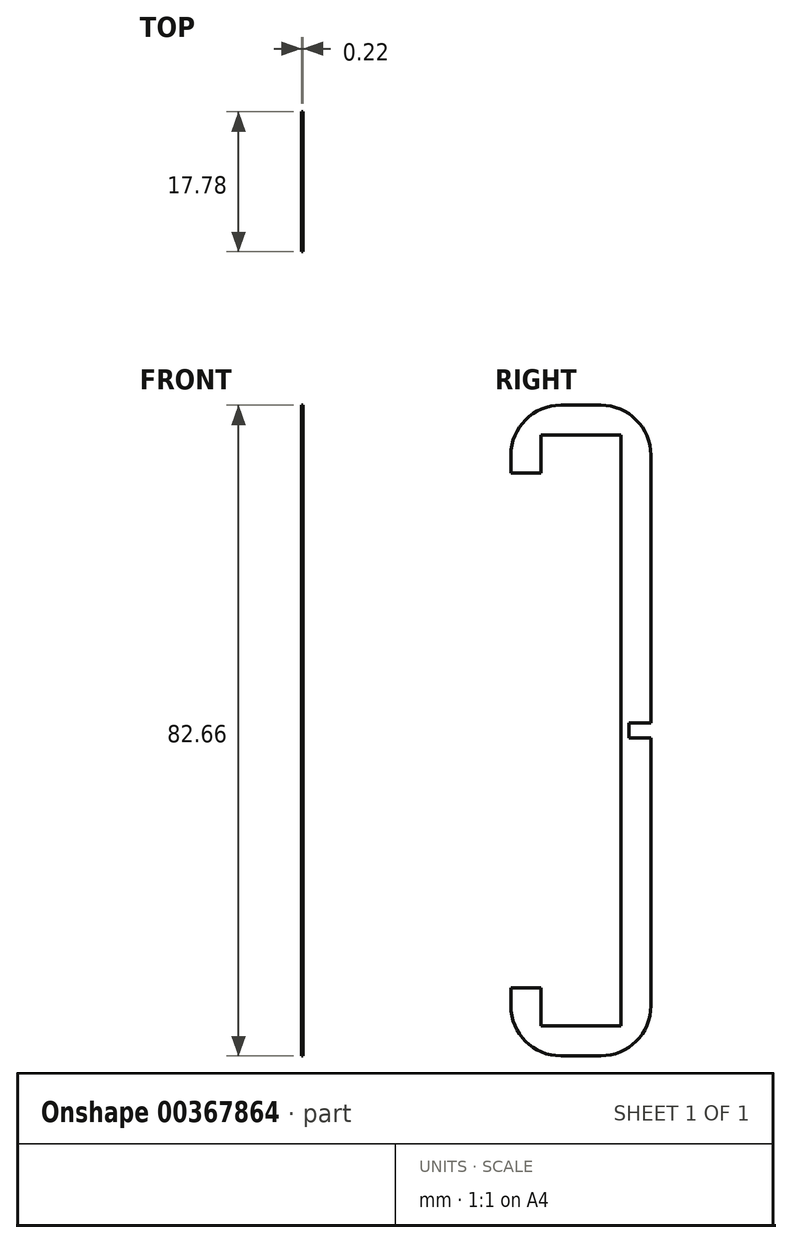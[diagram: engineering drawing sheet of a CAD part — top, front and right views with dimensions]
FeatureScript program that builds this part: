
annotation { "Feature Type Name" : "Feature", "Feature Type Description" : "" }
export const myFeature = defineFeature(function(context is Context, id is Id, definition is map)
    precondition{}
    {
        {
            var Q0;
            Q0=qCreatedBy(makeId("Right.planeOp"),FACE);
            var sketch = newSketch(context, id + "F0", { "sketchPlane" : qUnion([Q0])});
            skLineSegment(sketch, "E0", {"start": v(-8, 0) * mm, "end": v(-8, 37.52) * mm});
            skLineSegment(sketch, "E1", {"start": v(-8, 37.52) * mm, "end": v(-18.17, 37.52) * mm});
            skLineSegment(sketch, "E2", {"start": v(-18.17, 37.52) * mm, "end": v(-18.17, 32.7) * mm});
            skLineSegment(sketch, "E3", {"start": v(-18.17, 32.7) * mm, "end": v(-21.98, 32.7) * mm});
            skLineSegment(sketch, "E4", {"start": v(-21.98, 32.7) * mm, "end": v(-21.98, 34.98) * mm});
            skLineSegment(sketch, "E5", {"start": v(-15.63, 41.33) * mm, "end": v(-10.55, 41.33) * mm});
            skLineSegment(sketch, "E6", {"start": v(-4.2, 34.98) * mm, "end": v(-4.2, 0) * mm});
            skPoint(sketch, "E7.visualSharp", {"position": v(-21.98, 41.33) * mm});
            skArc(sketch, "E7.filletArc", {"start": v(-15.63, 41.33) * mm, "mid": v(-20.12, 39.47) * mm, "end": v(-21.98, 34.98) * mm});
            skPoint(sketch, "E8.visualSharp", {"position": v(-4.2, 41.33) * mm});
            skArc(sketch, "E8.filletArc", {"start": v(-4.2, 34.98) * mm, "mid": v(-6.06, 39.47) * mm, "end": v(-10.55, 41.33) * mm});
            skLineSegment(sketch, "E9.MirrorCS", {"start": v(-18.17, -37.52) * mm, "end": v(-18.17, -32.7) * mm});
            skLineSegment(sketch, "E10.MirrorCS", {"start": v(-21.98, -32.7) * mm, "end": v(-21.98, -34.98) * mm});
            skLineSegment(sketch, "E11.MirrorCS", {"start": v(-8, -37.52) * mm, "end": v(-18.17, -37.52) * mm});
            skPoint(sketch, "E12.MirrorP", {"position": v(-4.2, -41.33) * mm});
            skArc(sketch, "E13.MirrorCS", {"start": v(-15.63, -41.33) * mm, "mid": v(-20.12, -39.47) * mm, "end": v(-21.98, -34.98) * mm});
            skLineSegment(sketch, "E14.MirrorCS", {"start": v(-18.17, -32.7) * mm, "end": v(-21.98, -32.7) * mm});
            skArc(sketch, "E15.MirrorCS", {"start": v(-4.2, -34.98) * mm, "mid": v(-6.06, -39.47) * mm, "end": v(-10.55, -41.33) * mm});
            skPoint(sketch, "E16.MirrorP", {"position": v(-21.98, -41.33) * mm});
            skLineSegment(sketch, "E17.MirrorCS", {"start": v(-15.63, -41.33) * mm, "end": v(-10.55, -41.33) * mm});
            skLineSegment(sketch, "E18.MirrorCS", {"start": v(-8, 0) * mm, "end": v(-8, -37.52) * mm});
            skLineSegment(sketch, "E19.MirrorCS", {"start": v(-4.2, -34.98) * mm, "end": v(-4.2, 0) * mm});
            skSolve(sketch);
        }
        {
            var Q0;
            Q0=makeQuery(id+"F0.imprint","IMPRINT",FACE,{"disambiguationData":[TD([[makeQuery(id+"F0.imprint","IMPRINT",EDGE,{"derivedFrom":sQuery(id+"F0.wireOp",EDGE,"E0")}),-1.0]])]});
            extrude(context, id + "F1", {"entities" : qUnion([Q0]), "depth" : 5.73 / 50.8 * mm, "hasSecondDirection" : true, "secondDirectionOppositeDirection" : true, "secondDirectionDepth" : 5.73 / 50.8 * mm});
        }
        {
            var Q0;
            Q0=makeQuery(id+"F1.opExtrude","SWEPT_FACE",FACE,{"disambiguationData":[OSD([sQuery(id+"F0.wireOp",EDGE,"E6"),sQuery(id+"F0.wireOp",EDGE,"E19.MirrorCS")])]});
            var sketch = newSketch(context, id + "F2", { "sketchPlane" : qUnion([Q0])});
            skCircle(sketch, "E20", {"center": v(0, 0) * mm, "radius": 0.95 * mm});
            skSolve(sketch);
        }
        {
            var Q0;
            Q0=makeQuery(id+"F2.imprint","IMPRINT",FACE,{"disambiguationData":[TD([[makeQuery(id+"F2.imprint","IMPRINT",EDGE,{"derivedFrom":sQuery(id+"F2.wireOp",EDGE,"E20")}),1.0]])]});
            extrude(context, id + "F3", {"entities" : qUnion([Q0]), "operationType" : NewBodyOperationType.REMOVE, "oppositeDirection" : true, "depth" : 2.8 * mm});
        }
    });
